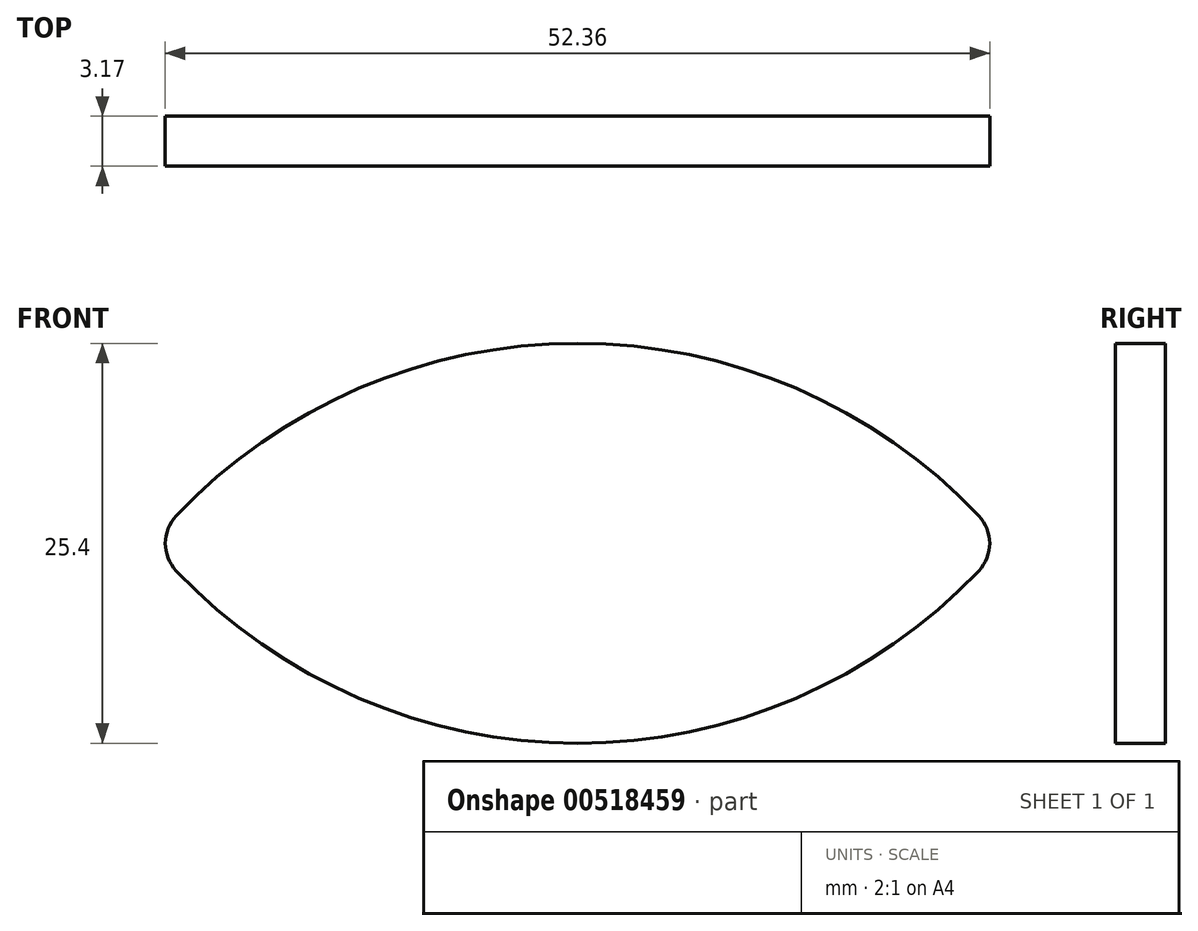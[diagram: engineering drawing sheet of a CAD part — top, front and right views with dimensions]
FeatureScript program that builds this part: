
annotation { "Feature Type Name" : "Feature", "Feature Type Description" : "" }
export const myFeature = defineFeature(function(context is Context, id is Id, definition is map)
    precondition{}
    {
        {
            var Q0;
            Q0=qCreatedBy(makeId("Front.planeOp"),FACE);
            var sketch = newSketch(context, id + "F0", { "sketchPlane" : qUnion([Q0])});
            skLineSegment(sketch, "E0", {"start": v(-288.6, -62.25) * mm, "end": v(-263.2, -62.25) * mm});
            skLineSegment(sketch, "E1", {"start": v(-275.9, -62.25) * mm, "end": v(-275.9, -51.65) * mm});
            skLineSegment(sketch, "E2", {"start": v(-242.95, -62.42) * mm, "end": v(-197.82, -62.42) * mm});
            skArc(sketch, "E3", {"start": v(-203.16, -23.4) * mm, "mid": v(-230.2, -10.7) * mm, "end": v(-257.22, -23.4) * mm});
            skArc(sketch, "E4", {"start": v(-257.22, -23.4) * mm, "mid": v(-230.2, -36.1) * mm, "end": v(-203.16, -23.4) * mm});
            skSolve(sketch);
        }
        {
            var Q0;
            Q0 = qSketchRegion(id + "F0", true);
            extrude(context, id + "F1", {"entities" : qUnion([Q0]), "depth" : 3.17 * mm, "offsetDistance" : 25.4 * mm});
        }
        {
            var Q0;
            {var subQ0=sQuery(id+"F0.wireOp",EDGE,"E4");var subQ1=sQuery(id+"F0.wireOp",EDGE,"E3");Q0=makeQuery(id+"F1.opExtrude","SWEPT_EDGE",EDGE,{"disambiguationData":[OSD([subQ1,subQ0]),TDD([makeQuery(id+"F0.imprint","INTERSECT",VERTEX,{"disambiguationData":[OD(0.0)],"derivedFrom":[subQ1,subQ0]})])]});}
            fillet(context, id + "F2", {"entities" : qUnion([Q0]), "radius" : 2.54 * mm, "tangentPropagation" : true, "allowEdgeOverflow" : false});
        }
        {
            var Q0;
            {var subQ0=sQuery(id+"F0.wireOp",EDGE,"E4");var subQ1=sQuery(id+"F0.wireOp",EDGE,"E3");Q0=makeQuery(id+"F1.opExtrude","SWEPT_EDGE",EDGE,{"disambiguationData":[OSD([subQ1,subQ0]),TDD([makeQuery(id+"F0.imprint","INTERSECT",VERTEX,{"disambiguationData":[OD(1.0)],"derivedFrom":[subQ1,subQ0]})])]});}
            fillet(context, id + "F3", {"entities" : qUnion([Q0]), "radius" : 2.54 * mm, "tangentPropagation" : true, "allowEdgeOverflow" : false});
        }
    });
